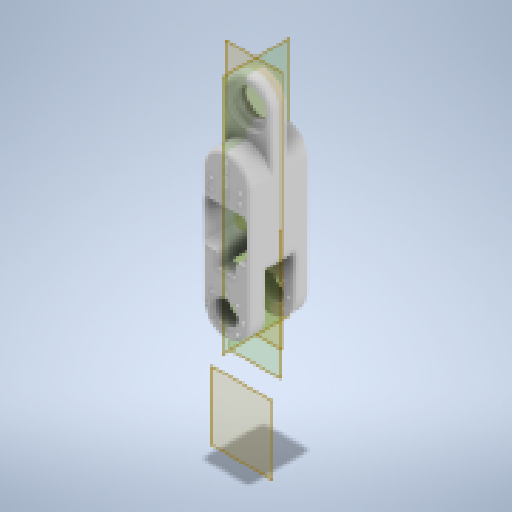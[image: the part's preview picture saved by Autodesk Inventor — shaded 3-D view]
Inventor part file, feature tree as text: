
AUTODESK INVENTOR PART (.ipt)
format: ipt  version: 2024 (Build 280153000, 153)  size: 1,674,240 bytes
history: native  units: mm
features: reference x32, extrude x11, sketch x11, other x7, projected_geometry x6, fillet x5, plane x4, move_body x4, mirror x3, direct_edit x3, chamfer x2
ambient origin geometry x8: Origin, YZ Plane, XZ Plane, XY Plane, X Axis, Y Axis, Z Axis, Center Point
bodies: Solid1 (feature_tree)
feature tree (88):
  plane  "Work Plane1"
  extrude  "Extrusion1"  Depth=15.0mm
  plane  "Work Plane2"
  mirror  "Mirror1"
  extrude  "Extrusion3"  Depth=10.0mm
  extrude  "Extrusion5"  Depth=50.0mm
  chamfer  "Chamfer1"  Distance=18.0mm
  chamfer  "Chamfer2"  Distance=50.0mm Angle=45.0deg
  extrude  "Extrusion6"  Depth=2.0mm
  extrude  "Extrusion7"  Depth=6.0mm TaperAngle=0.0deg
  extrude  "Extrusion8"  Depth=6.0mm TaperAngle=0.0deg
  extrude  "Extrusion9"  Depth=10.0mm
  plane  "Work Plane3"
  mirror  "Mirror2"
  extrude  "Extrusion10"  Depth=10.0mm TaperAngle=0.0deg
  fillet  "Fillet1"  Radius=38.0mm
  fillet  "Fillet2"  Radius=3.0mm
  fillet  "Fillet3"  Radius=27.0mm
  fillet  "Fillet5"  Radius=6.0mm
  direct_edit  "Direct Edit1"
  extrude  "Extrusion11"  Depth=10.0mm
  extrude  "Extrusion13"  TaperAngle=0.0deg  [1 undecoded]
  fillet  "Fillet6"  Radius=25.0mm
  plane  "Work Plane4"
  direct_edit  "Direct Edit2"
  direct_edit  "Direct Edit3"
  extrude  "Extrusion14"  Depth=25.0mm
  mirror  "Mirror5"
  sketch  "Sketch1"  dims[d3=18.0mm d4=0.0mm d5=15.0mm]
  sketch  "Sketch3"  dims[d9=10.0mm d10=0.0mm d13=50.0mm]
  reference  "Reference4"
  reference  "Reference5"
  reference  "Reference6"
  reference  "Reference7"
  reference  "Reference8"
  reference  "Reference9"
  reference  "Reference10"
  reference  "Reference11"
  reference  "Reference13"
  reference  "Reference14"
  sketch  "Sketch5"  dims[d14=150.0mm d15=50.0mm]
  reference  "Reference15"
  projected_geometry  "Projected Loop2"
  sketch  "Sketch8"  dims[d16=10.0mm d17=18.0mm d18=0.0mm]
  reference  "Reference16"
  reference  "Reference17"
  reference  "Reference18"
  reference  "Reference19"
  reference  "Reference20"
  reference  "Reference21"
  reference  "Reference22"
  reference  "Reference23"
  reference  "Reference24"
  reference  "Reference25"
  reference  "Reference26"
  reference  "Reference27"
  reference  "Reference28"
  sketch  "Sketch9"  dims[d19=10.0mm]
  reference  "Reference29"
  reference  "Reference30"
  reference  "Reference31"
  reference  "Reference32"
  reference  "Reference33"
  reference  "Reference34"
  reference  "Reference35"
  reference  "Reference36"
  sketch  "Sketch10"  dims[d20=10.0mm]
  sketch  "Sketch11"  dims[d21=10.0mm d22=50.0mm d23=8.0mm d24=45.0deg]
  projected_geometry  "Projected Loop3"
  sketch  "Sketch12"  dims[d25=8.0mm d26=50.0mm d27=45.0deg d28=2.0mm]
  projected_geometry  "Projected Loop4"
  projected_geometry  "Projected Loop5"
  sketch  "Sketch13"  dims[d29=4.2mm d30=6.0mm d31=0.0mm]
  sketch  "Sketch15"  dims[d32=2.0mm d33=6.0mm d34=0.0mm]
  projected_geometry  "Projected Loop6"
  sketch  "Sketch16"  dims[d35=10.0mm d36=60.0mm d39=10.0mm d40=0.0mm d41=38.0mm d42=3.0mm d43=27.0mm d44=6.0mm d45=0.0mm d46=30.0mm d47=0.0mm d48=0.0mm d49=25.0mm d50=25.0mm d51=4.0mm d53=4.0mm d54=0.0mm d55=0.0mm d56=-0.25mm d57=0.0mm d58=0.0mm d59=-0.25mm d60=1.5mm d61=0.0mm d66=16.0mm d67=20.0mm d68=10.0mm d69=0.0mm d70=3.0mm d71=0.0mm d72=0.0mm d73=-0.75mm d74=0.0mm d75=0.0mm d76=-0.75mm d80=3.9mm d81=3.9mm d82=10.0mm d83=5.564971mm d84=5.564971mm d85=132.668895mm d86=0.0mm d87=0.0mm]
  projected_geometry  "Projected Loop8"
  other  "<userpath>\Documents\Inventor\robot arm\arms\arms.iam"
  other  "arms.iam"
  other  "middle arm pulley:1"
  other  "middle arm pulley:2"
  other  "lower arm with pulley:1"
  other  "lower arm:1"
  other  "stepper motor:3"
  move_body  "Move1"
  move_body  "Move2"
  move_body  "Move3"
  move_body  "Move4"
note: 1 required parameter value undecoded (feature->parameter linkage not recoverable at this tier; creation-order binding heuristic only, values carry confidence <= 0.55)
